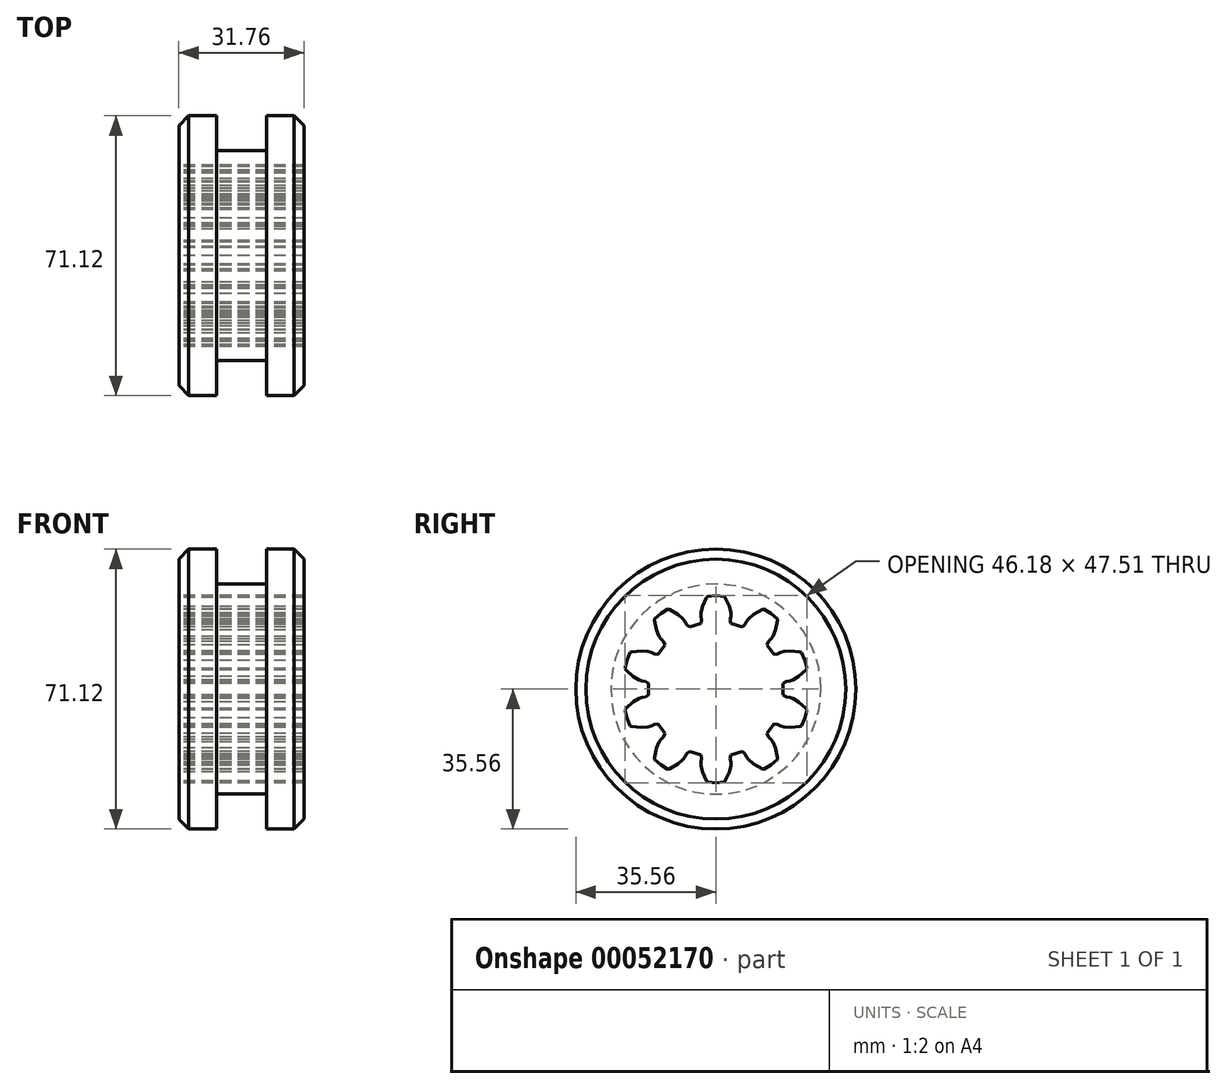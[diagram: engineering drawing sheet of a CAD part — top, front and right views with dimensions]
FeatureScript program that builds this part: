
annotation { "Feature Type Name" : "Feature", "Feature Type Description" : "" }
export const myFeature = defineFeature(function(context is Context, id is Id, definition is map)
    precondition{}
    {
        {
            var Q0;
            Q0=qCreatedBy(makeId("Right.planeOp"),FACE);
            var sketch = newSketch(context, id + "F0", { "sketchPlane" : qUnion([Q0])});
            skLineSegment(sketch, "E0", {"start": v(-23.1, 5.26) * mm, "end": v(-22.6, 7.34) * mm});
            skLineSegment(sketch, "E1", {"start": v(-22.6, 7.34) * mm, "end": v(-21.78, 9.31) * mm});
            skLineSegment(sketch, "E2", {"start": v(-21.78, 9.31) * mm, "end": v(-21.4, 9.44) * mm});
            skLineSegment(sketch, "E3", {"start": v(-21.4, 9.44) * mm, "end": v(-18.92, 9.74) * mm});
            skLineSegment(sketch, "E4", {"start": v(-18.92, 9.74) * mm, "end": v(-17.24, 9.59) * mm});
            skLineSegment(sketch, "E5", {"start": v(-17.24, 9.59) * mm, "end": v(-16.42, 9.34) * mm});
            skLineSegment(sketch, "E6", {"start": v(-16.42, 9.34) * mm, "end": v(-15.64, 8.9) * mm});
            skLineSegment(sketch, "E7", {"start": v(-15.64, 8.9) * mm, "end": v(-14.71, 8.81) * mm});
            skLineSegment(sketch, "E8", {"start": v(-14.71, 8.81) * mm, "end": v(-12.93, 11.27) * mm});
            skLineSegment(sketch, "E9", {"start": v(-12.93, 11.27) * mm, "end": v(-13.3, 12.12) * mm});
            skLineSegment(sketch, "E10", {"start": v(-13.3, 12.12) * mm, "end": v(-13.95, 12.73) * mm});
            skLineSegment(sketch, "E11", {"start": v(-13.95, 12.73) * mm, "end": v(-14.45, 13.43) * mm});
            skLineSegment(sketch, "E12", {"start": v(-14.45, 13.43) * mm, "end": v(-15.1, 14.98) * mm});
            skLineSegment(sketch, "E13", {"start": v(-15.1, 14.98) * mm, "end": v(-15.6, 17.44) * mm});
            skLineSegment(sketch, "E14", {"start": v(-15.6, 17.44) * mm, "end": v(-15.59, 17.83) * mm});
            skLineSegment(sketch, "E15", {"start": v(-15.59, 17.83) * mm, "end": v(-13.96, 19.22) * mm});
            skLineSegment(sketch, "E16", {"start": v(-13.96, 19.22) * mm, "end": v(-12.14, 20.33) * mm});
            skLineSegment(sketch, "E17", {"start": v(-12.14, 20.33) * mm, "end": v(-11.77, 20.22) * mm});
            skLineSegment(sketch, "E18", {"start": v(-11.77, 20.22) * mm, "end": v(-9.58, 19) * mm});
            skLineSegment(sketch, "E19", {"start": v(-9.58, 19) * mm, "end": v(-8.31, 17.9) * mm});
            skLineSegment(sketch, "E20", {"start": v(-8.31, 17.9) * mm, "end": v(-7.8, 17.2) * mm});
            skLineSegment(sketch, "E21", {"start": v(-7.8, 17.2) * mm, "end": v(-7.42, 16.4) * mm});
            skLineSegment(sketch, "E22", {"start": v(-7.42, 16.4) * mm, "end": v(-6.72, 15.78) * mm});
            skLineSegment(sketch, "E23", {"start": v(-6.72, 15.78) * mm, "end": v(-3.83, 16.71) * mm});
            skLineSegment(sketch, "E24", {"start": v(-3.83, 16.71) * mm, "end": v(-3.63, 17.63) * mm});
            skLineSegment(sketch, "E25", {"start": v(-3.63, 17.63) * mm, "end": v(-3.8, 18.5) * mm});
            skLineSegment(sketch, "E26", {"start": v(-3.8, 18.5) * mm, "end": v(-3.8, 19.36) * mm});
            skLineSegment(sketch, "E27", {"start": v(-3.8, 19.36) * mm, "end": v(-3.42, 21) * mm});
            skLineSegment(sketch, "E28", {"start": v(-3.42, 21) * mm, "end": v(-2.36, 23.28) * mm});
            skLineSegment(sketch, "E29", {"start": v(-2.36, 23.28) * mm, "end": v(-2.13, 23.59) * mm});
            skLineSegment(sketch, "E30", {"start": v(-2.13, 23.59) * mm, "end": v(0, 23.76) * mm});
            skLineSegment(sketch, "E31", {"start": v(0, 23.76) * mm, "end": v(2.13, 23.59) * mm});
            skLineSegment(sketch, "E32", {"start": v(2.13, 23.59) * mm, "end": v(2.36, 23.28) * mm});
            skLineSegment(sketch, "E33", {"start": v(2.36, 23.28) * mm, "end": v(3.42, 21) * mm});
            skLineSegment(sketch, "E34", {"start": v(3.42, 21) * mm, "end": v(3.8, 19.36) * mm});
            skLineSegment(sketch, "E35", {"start": v(3.8, 19.36) * mm, "end": v(3.8, 18.5) * mm});
            skLineSegment(sketch, "E36", {"start": v(3.8, 18.5) * mm, "end": v(3.63, 17.63) * mm});
            skLineSegment(sketch, "E37", {"start": v(3.63, 17.63) * mm, "end": v(3.83, 16.71) * mm});
            skLineSegment(sketch, "E38", {"start": v(3.83, 16.71) * mm, "end": v(6.72, 15.78) * mm});
            skLineSegment(sketch, "E39", {"start": v(6.72, 15.78) * mm, "end": v(7.42, 16.4) * mm});
            skLineSegment(sketch, "E40", {"start": v(7.42, 16.4) * mm, "end": v(7.8, 17.2) * mm});
            skLineSegment(sketch, "E41", {"start": v(7.8, 17.2) * mm, "end": v(8.31, 17.9) * mm});
            skLineSegment(sketch, "E42", {"start": v(8.31, 17.9) * mm, "end": v(9.58, 19) * mm});
            skLineSegment(sketch, "E43", {"start": v(9.58, 19) * mm, "end": v(11.77, 20.22) * mm});
            skLineSegment(sketch, "E44", {"start": v(11.77, 20.22) * mm, "end": v(12.14, 20.33) * mm});
            skLineSegment(sketch, "E45", {"start": v(12.14, 20.33) * mm, "end": v(13.96, 19.22) * mm});
            skLineSegment(sketch, "E46", {"start": v(13.96, 19.22) * mm, "end": v(15.59, 17.83) * mm});
            skLineSegment(sketch, "E47", {"start": v(15.59, 17.83) * mm, "end": v(15.6, 17.44) * mm});
            skLineSegment(sketch, "E48", {"start": v(15.6, 17.44) * mm, "end": v(15.1, 14.98) * mm});
            skLineSegment(sketch, "E49", {"start": v(15.1, 14.98) * mm, "end": v(14.45, 13.43) * mm});
            skLineSegment(sketch, "E50", {"start": v(14.45, 13.43) * mm, "end": v(13.95, 12.73) * mm});
            skLineSegment(sketch, "E51", {"start": v(13.95, 12.73) * mm, "end": v(13.3, 12.12) * mm});
            skLineSegment(sketch, "E52", {"start": v(13.3, 12.12) * mm, "end": v(12.93, 11.27) * mm});
            skLineSegment(sketch, "E53", {"start": v(12.93, 11.27) * mm, "end": v(14.71, 8.81) * mm});
            skLineSegment(sketch, "E54", {"start": v(14.71, 8.81) * mm, "end": v(15.64, 8.9) * mm});
            skLineSegment(sketch, "E55", {"start": v(15.64, 8.9) * mm, "end": v(16.42, 9.34) * mm});
            skLineSegment(sketch, "E56", {"start": v(16.42, 9.34) * mm, "end": v(17.24, 9.59) * mm});
            skLineSegment(sketch, "E57", {"start": v(17.24, 9.59) * mm, "end": v(18.92, 9.74) * mm});
            skLineSegment(sketch, "E58", {"start": v(18.92, 9.74) * mm, "end": v(21.4, 9.44) * mm});
            skLineSegment(sketch, "E59", {"start": v(21.4, 9.44) * mm, "end": v(21.78, 9.31) * mm});
            skLineSegment(sketch, "E60", {"start": v(21.78, 9.31) * mm, "end": v(22.6, 7.34) * mm});
            skLineSegment(sketch, "E61", {"start": v(22.6, 7.34) * mm, "end": v(23.1, 5.26) * mm});
            skLineSegment(sketch, "E62", {"start": v(23.1, 5.26) * mm, "end": v(22.87, 4.95) * mm});
            skLineSegment(sketch, "E63", {"start": v(22.87, 4.95) * mm, "end": v(21.03, 3.24) * mm});
            skLineSegment(sketch, "E64", {"start": v(21.03, 3.24) * mm, "end": v(19.58, 2.38) * mm});
            skLineSegment(sketch, "E65", {"start": v(19.58, 2.38) * mm, "end": v(18.77, 2.1) * mm});
            skLineSegment(sketch, "E66", {"start": v(18.77, 2.1) * mm, "end": v(17.89, 2) * mm});
            skLineSegment(sketch, "E67", {"start": v(17.89, 2) * mm, "end": v(17.08, 1.52) * mm});
            skLineSegment(sketch, "E68", {"start": v(17.08, 1.52) * mm, "end": v(17.08, -1.52) * mm});
            skLineSegment(sketch, "E69", {"start": v(17.08, -1.52) * mm, "end": v(17.89, -2) * mm});
            skLineSegment(sketch, "E70", {"start": v(17.89, -2) * mm, "end": v(18.77, -2.1) * mm});
            skLineSegment(sketch, "E71", {"start": v(18.77, -2.1) * mm, "end": v(19.58, -2.38) * mm});
            skLineSegment(sketch, "E72", {"start": v(19.58, -2.38) * mm, "end": v(21.03, -3.24) * mm});
            skLineSegment(sketch, "E73", {"start": v(21.03, -3.24) * mm, "end": v(22.87, -4.95) * mm});
            skLineSegment(sketch, "E74", {"start": v(22.87, -4.95) * mm, "end": v(23.1, -5.26) * mm});
            skLineSegment(sketch, "E75", {"start": v(23.1, -5.26) * mm, "end": v(22.6, -7.34) * mm});
            skLineSegment(sketch, "E76", {"start": v(22.6, -7.34) * mm, "end": v(21.78, -9.31) * mm});
            skLineSegment(sketch, "E77", {"start": v(21.78, -9.31) * mm, "end": v(21.4, -9.44) * mm});
            skLineSegment(sketch, "E78", {"start": v(21.4, -9.44) * mm, "end": v(18.92, -9.74) * mm});
            skLineSegment(sketch, "E79", {"start": v(18.92, -9.74) * mm, "end": v(17.24, -9.59) * mm});
            skLineSegment(sketch, "E80", {"start": v(17.24, -9.59) * mm, "end": v(16.42, -9.34) * mm});
            skLineSegment(sketch, "E81", {"start": v(16.42, -9.34) * mm, "end": v(15.64, -8.9) * mm});
            skLineSegment(sketch, "E82", {"start": v(15.64, -8.9) * mm, "end": v(14.71, -8.81) * mm});
            skLineSegment(sketch, "E83", {"start": v(14.71, -8.81) * mm, "end": v(12.93, -11.27) * mm});
            skLineSegment(sketch, "E84", {"start": v(12.93, -11.27) * mm, "end": v(13.3, -12.12) * mm});
            skLineSegment(sketch, "E85", {"start": v(13.3, -12.12) * mm, "end": v(13.95, -12.73) * mm});
            skLineSegment(sketch, "E86", {"start": v(13.95, -12.73) * mm, "end": v(14.45, -13.43) * mm});
            skLineSegment(sketch, "E87", {"start": v(14.45, -13.43) * mm, "end": v(15.1, -14.98) * mm});
            skLineSegment(sketch, "E88", {"start": v(15.1, -14.98) * mm, "end": v(15.6, -17.44) * mm});
            skLineSegment(sketch, "E89", {"start": v(15.6, -17.44) * mm, "end": v(15.59, -17.83) * mm});
            skLineSegment(sketch, "E90", {"start": v(15.59, -17.83) * mm, "end": v(13.96, -19.22) * mm});
            skLineSegment(sketch, "E91", {"start": v(13.96, -19.22) * mm, "end": v(12.14, -20.33) * mm});
            skLineSegment(sketch, "E92", {"start": v(12.14, -20.33) * mm, "end": v(11.77, -20.22) * mm});
            skLineSegment(sketch, "E93", {"start": v(11.77, -20.22) * mm, "end": v(9.58, -19) * mm});
            skLineSegment(sketch, "E94", {"start": v(9.58, -19) * mm, "end": v(8.31, -17.9) * mm});
            skLineSegment(sketch, "E95", {"start": v(8.31, -17.9) * mm, "end": v(7.8, -17.2) * mm});
            skLineSegment(sketch, "E96", {"start": v(7.8, -17.2) * mm, "end": v(7.42, -16.4) * mm});
            skLineSegment(sketch, "E97", {"start": v(7.42, -16.4) * mm, "end": v(6.72, -15.78) * mm});
            skLineSegment(sketch, "E98", {"start": v(6.72, -15.78) * mm, "end": v(3.83, -16.71) * mm});
            skLineSegment(sketch, "E99", {"start": v(3.83, -16.71) * mm, "end": v(3.63, -17.63) * mm});
            skLineSegment(sketch, "E100", {"start": v(3.63, -17.63) * mm, "end": v(3.8, -18.5) * mm});
            skLineSegment(sketch, "E101", {"start": v(3.8, -18.5) * mm, "end": v(3.8, -19.36) * mm});
            skLineSegment(sketch, "E102", {"start": v(3.8, -19.36) * mm, "end": v(3.42, -21) * mm});
            skLineSegment(sketch, "E103", {"start": v(3.42, -21) * mm, "end": v(2.36, -23.28) * mm});
            skLineSegment(sketch, "E104", {"start": v(2.36, -23.28) * mm, "end": v(2.13, -23.59) * mm});
            skLineSegment(sketch, "E105", {"start": v(2.13, -23.59) * mm, "end": v(0, -23.76) * mm});
            skLineSegment(sketch, "E106", {"start": v(0, -23.76) * mm, "end": v(-2.13, -23.59) * mm});
            skLineSegment(sketch, "E107", {"start": v(-2.13, -23.59) * mm, "end": v(-2.36, -23.28) * mm});
            skLineSegment(sketch, "E108", {"start": v(-2.36, -23.28) * mm, "end": v(-3.42, -21) * mm});
            skLineSegment(sketch, "E109", {"start": v(-3.42, -21) * mm, "end": v(-3.8, -19.36) * mm});
            skLineSegment(sketch, "E110", {"start": v(-3.8, -19.36) * mm, "end": v(-3.8, -18.5) * mm});
            skLineSegment(sketch, "E111", {"start": v(-3.8, -18.5) * mm, "end": v(-3.63, -17.63) * mm});
            skLineSegment(sketch, "E112", {"start": v(-3.63, -17.63) * mm, "end": v(-3.83, -16.71) * mm});
            skLineSegment(sketch, "E113", {"start": v(-3.83, -16.71) * mm, "end": v(-6.72, -15.78) * mm});
            skLineSegment(sketch, "E114", {"start": v(-6.72, -15.78) * mm, "end": v(-7.42, -16.4) * mm});
            skLineSegment(sketch, "E115", {"start": v(-7.42, -16.4) * mm, "end": v(-7.8, -17.2) * mm});
            skLineSegment(sketch, "E116", {"start": v(-7.8, -17.2) * mm, "end": v(-8.31, -17.9) * mm});
            skLineSegment(sketch, "E117", {"start": v(-8.31, -17.9) * mm, "end": v(-9.58, -19) * mm});
            skLineSegment(sketch, "E118", {"start": v(-9.58, -19) * mm, "end": v(-11.77, -20.22) * mm});
            skLineSegment(sketch, "E119", {"start": v(-11.77, -20.22) * mm, "end": v(-12.14, -20.33) * mm});
            skLineSegment(sketch, "E120", {"start": v(-12.14, -20.33) * mm, "end": v(-13.96, -19.22) * mm});
            skLineSegment(sketch, "E121", {"start": v(-13.96, -19.22) * mm, "end": v(-15.59, -17.83) * mm});
            skLineSegment(sketch, "E122", {"start": v(-15.59, -17.83) * mm, "end": v(-15.6, -17.44) * mm});
            skLineSegment(sketch, "E123", {"start": v(-15.6, -17.44) * mm, "end": v(-15.1, -14.98) * mm});
            skLineSegment(sketch, "E124", {"start": v(-15.1, -14.98) * mm, "end": v(-14.45, -13.43) * mm});
            skLineSegment(sketch, "E125", {"start": v(-14.45, -13.43) * mm, "end": v(-13.95, -12.73) * mm});
            skLineSegment(sketch, "E126", {"start": v(-13.95, -12.73) * mm, "end": v(-13.3, -12.12) * mm});
            skLineSegment(sketch, "E127", {"start": v(-13.3, -12.12) * mm, "end": v(-12.93, -11.27) * mm});
            skLineSegment(sketch, "E128", {"start": v(-12.93, -11.27) * mm, "end": v(-14.71, -8.81) * mm});
            skLineSegment(sketch, "E129", {"start": v(-14.71, -8.81) * mm, "end": v(-15.64, -8.9) * mm});
            skLineSegment(sketch, "E130", {"start": v(-15.64, -8.9) * mm, "end": v(-16.42, -9.34) * mm});
            skLineSegment(sketch, "E131", {"start": v(-16.42, -9.34) * mm, "end": v(-17.24, -9.59) * mm});
            skLineSegment(sketch, "E132", {"start": v(-17.24, -9.59) * mm, "end": v(-18.92, -9.74) * mm});
            skLineSegment(sketch, "E133", {"start": v(-18.92, -9.74) * mm, "end": v(-21.4, -9.44) * mm});
            skLineSegment(sketch, "E134", {"start": v(-21.4, -9.44) * mm, "end": v(-21.78, -9.31) * mm});
            skLineSegment(sketch, "E135", {"start": v(-21.78, -9.31) * mm, "end": v(-22.6, -7.34) * mm});
            skLineSegment(sketch, "E136", {"start": v(-22.6, -7.34) * mm, "end": v(-23.1, -5.26) * mm});
            skLineSegment(sketch, "E137", {"start": v(-23.1, -5.26) * mm, "end": v(-22.87, -4.95) * mm});
            skLineSegment(sketch, "E138", {"start": v(-22.87, -4.95) * mm, "end": v(-21.03, -3.24) * mm});
            skLineSegment(sketch, "E139", {"start": v(-21.03, -3.24) * mm, "end": v(-19.58, -2.38) * mm});
            skLineSegment(sketch, "E140", {"start": v(-19.58, -2.38) * mm, "end": v(-18.77, -2.1) * mm});
            skLineSegment(sketch, "E141", {"start": v(-18.77, -2.1) * mm, "end": v(-17.89, -2) * mm});
            skLineSegment(sketch, "E142", {"start": v(-17.89, -2) * mm, "end": v(-17.08, -1.52) * mm});
            skLineSegment(sketch, "E143", {"start": v(-17.08, -1.52) * mm, "end": v(-17.08, 1.52) * mm});
            skLineSegment(sketch, "E144", {"start": v(-17.08, 1.52) * mm, "end": v(-17.89, 2) * mm});
            skLineSegment(sketch, "E145", {"start": v(-17.89, 2) * mm, "end": v(-18.77, 2.1) * mm});
            skLineSegment(sketch, "E146", {"start": v(-18.77, 2.1) * mm, "end": v(-19.58, 2.38) * mm});
            skLineSegment(sketch, "E147", {"start": v(-19.58, 2.38) * mm, "end": v(-21.03, 3.24) * mm});
            skLineSegment(sketch, "E148", {"start": v(-21.03, 3.24) * mm, "end": v(-22.87, 4.95) * mm});
            skLineSegment(sketch, "E149", {"start": v(-22.87, 4.95) * mm, "end": v(-23.1, 5.26) * mm});
            skCircle(sketch, "E150", {"center": v(0, 0) * mm, "radius": 35.56 * mm});
            skSolve(sketch);
        }
        {
            var Q0;
            Q0=makeQuery(id+"F0.imprint","IMPRINT",FACE,{"disambiguationData":[TD([[makeQuery(id+"F0.imprint","IMPRINT",EDGE,{"derivedFrom":sQuery(id+"F0.wireOp",EDGE,"E0")}),1.0]])]});
            extrude(context, id + "F1", {"entities" : qUnion([Q0]), "endBound" : BoundingType.SYMMETRIC, "depth" : 31.75 * mm});
        }
        {
            var Q0;
            Q0=makeQuery(id+"F1.opExtrude","CAP_EDGE",EDGE,{"disambiguationData":[OSD([sQuery(id+"F0.wireOp",EDGE,"E150")])],"isStart":false});
            var Q1;
            Q1=makeQuery(id+"F1.opExtrude","CAP_EDGE",EDGE,{"disambiguationData":[OSD([sQuery(id+"F0.wireOp",EDGE,"E150")])],"isStart":true});
            chamfer(context, id + "F2", {"entities" : qUnion([Q0, Q1]), "width" : 2.54 * mm, "tangentPropagation" : true});
        }
        {
            var Q0;
            Q0=qCreatedBy(makeId("Right.planeOp"),FACE);
            var sketch = newSketch(context, id + "F3", { "sketchPlane" : qUnion([Q0])});
            skCircle(sketch, "E151", {"center": v(0, 0) * mm, "radius": 26.67 * mm});
            skCircle(sketch, "E152", {"center": v(0, 0) * mm, "radius": 35.56 * mm});
            skSolve(sketch);
        }
        {
            var Q0;
            Q0=qSketchRegion(id+"F3",true);
            extrude(context, id + "F4", {"entities" : qUnion([Q0]), "operationType" : NewBodyOperationType.REMOVE, "endBound" : BoundingType.SYMMETRIC, "oppositeDirection" : true, "depth" : 12.7 * mm});
        }
    });
